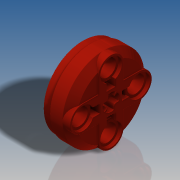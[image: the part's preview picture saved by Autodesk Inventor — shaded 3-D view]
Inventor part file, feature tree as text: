
AUTODESK INVENTOR PART (.ipt)
format: ipt  version: 2016 SP2 (Build 200236200, 236)  size: 533,504 bytes
history: native  units: in
note: dims shown in document units (in); Inventor stores cm internally (conversion verified against a paired STEP export)
features: extrude x5, sketch x2, revolve x1, fillet x1
ambient origin geometry x8: Origin, YZ Plane, XZ Plane, XY Plane, X Axis, Y Axis, Z Axis, Center Point
bodies: Solid1 (feature_tree)
feature tree (9):
  revolve  "Revolution1"  [1 undecoded]
  sketch  "Sketch3"  dims[d2=0.8819in d3=0.8504in d4=0.9134in d5=0.1575in d6=0.189in d7=0.2441in d8=0.2205in d9=0.0787in d10=45.0deg d11=90.0deg d12=0.2835in d13=0.2441in d14=0.189in d15=0.126in d16=0.126in d17=0.126in d18=0.126in d19=0.189in d20=0.0964in d21=45.0deg d22=0.1938in d23=0.1113in d24=0.0798in d25=0.0252in d26=0.0079in d27=0.0in d28=0.0079in d29=0.0in d30=0.0315in d31=0.0in d32=0.0315in d33=0.0in d34=0.1181in d35=0.0in d36=0.0039in]
  extrude  "Extrusion1"  Depth=0.0039in
  extrude  "Extrusion2"  Depth=0.0039in
  extrude  "Extrusion3"  Depth=0.0039in
  extrude  "Extrusion4"  Depth=0.0039in
  extrude  "Extrusion5"  Depth=0.0039in
  fillet  "Fillet1"  Radius=0.2205in
  sketch  "Sketch2"  dims[d0=0.378in d1=0.4094in]
note: 1 required parameter value undecoded (feature->parameter linkage not recoverable at this tier; creation-order binding heuristic only, values carry confidence <= 0.55)
